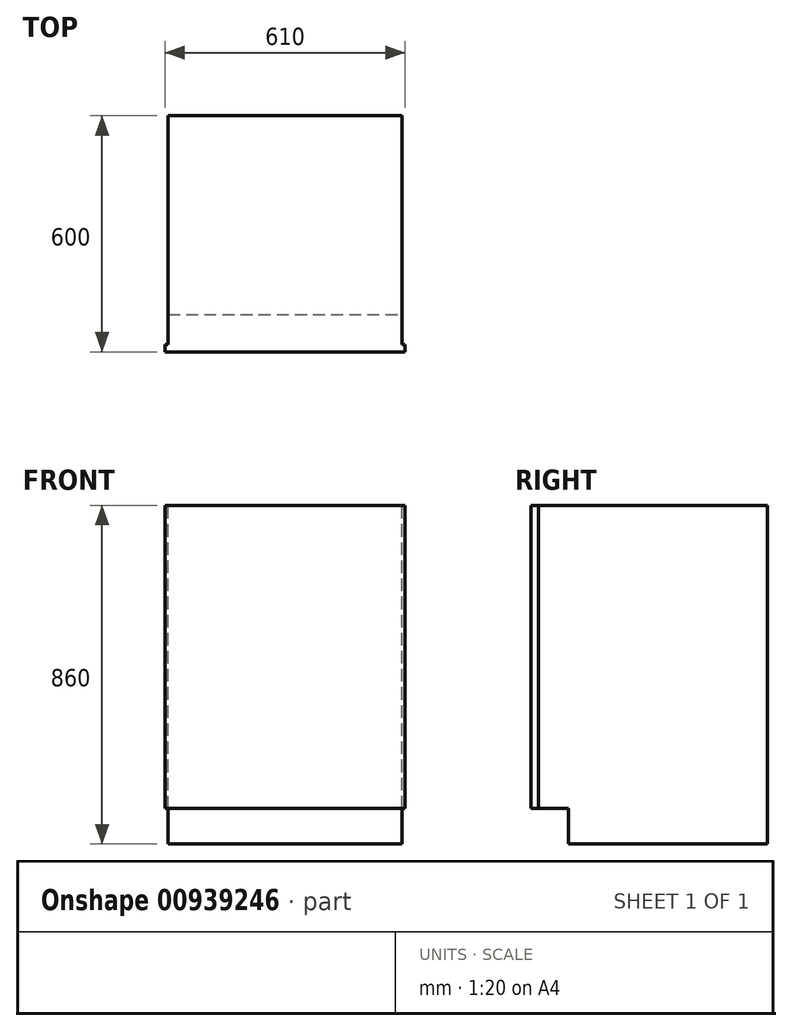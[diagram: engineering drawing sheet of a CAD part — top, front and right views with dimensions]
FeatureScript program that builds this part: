
annotation { "Feature Type Name" : "Feature", "Feature Type Description" : "" }
export const myFeature = defineFeature(function(context is Context, id is Id, definition is map)
    precondition{}
    {
        {
            var Q0;
            Q0=qCreatedBy(makeId("Front.planeOp"),FACE);
            var sketch = newSketch(context, id + "F0", { "sketchPlane" : qUnion([Q0])});
            skLineSegment(sketch, "E0.bottom", {"start": v(0, 0) * mm, "end": v(594, 0) * mm});
            skLineSegment(sketch, "E0.top", {"start": v(0, 860) * mm, "end": v(594, 860) * mm});
            skLineSegment(sketch, "E0.left", {"start": v(0, 0) * mm, "end": v(0, 860) * mm});
            skLineSegment(sketch, "E0.right", {"start": v(594, 0) * mm, "end": v(594, 860) * mm});
            skSolve(sketch);
        }
        {
            var Q0;
            Q0 = qSketchRegion(id + "F0", true);
            extrude(context, id + "F1", {"entities" : qUnion([Q0]), "depth" : 600 * mm, "offsetDistance" : 25 * mm});
        }
        {
            var Q0;
            Q0=makeQuery(id+"F1.opExtrude","CAP_FACE",FACE,{"disambiguationData":[OSD([sQuery(id+"F0.wireOp",EDGE,"E0.bottom"),sQuery(id+"F0.wireOp",EDGE,"E0.top"),sQuery(id+"F0.wireOp",EDGE,"E0.left"),sQuery(id+"F0.wireOp",EDGE,"E0.right")])],"isStart":false});
            var sketch = newSketch(context, id + "F2", { "sketchPlane" : qUnion([Q0])});
            skLineSegment(sketch, "E1.bottom", {"start": v(0, 0) * mm, "end": v(-8, 0) * mm});
            skLineSegment(sketch, "E1.top", {"start": v(0, 860) * mm, "end": v(-8, 860) * mm});
            skLineSegment(sketch, "E1.left", {"start": v(0, 0) * mm, "end": v(0, 860) * mm});
            skLineSegment(sketch, "E1.right", {"start": v(-8, 0) * mm, "end": v(-8, 860) * mm});
            skLineSegment(sketch, "E2", {"start": v(297, 0) * mm, "end": v(297, 939.39) * mm, "construction": true});
            skLineSegment(sketch, "E3.MirrorCS", {"start": v(602, 0) * mm, "end": v(602, 860) * mm});
            skLineSegment(sketch, "E4.MirrorCS", {"start": v(594, 860) * mm, "end": v(602, 860) * mm});
            skLineSegment(sketch, "E5.MirrorCS", {"start": v(594, 0) * mm, "end": v(594, 860) * mm});
            skLineSegment(sketch, "E6.MirrorCS", {"start": v(594, 0) * mm, "end": v(602, 0) * mm});
            skSolve(sketch);
        }
        {
            var Q0;
            Q0 = qSketchRegion(id + "F2", true);
            extrude(context, id + "F3", {"entities" : qUnion([Q0]), "operationType" : NewBodyOperationType.ADD, "oppositeDirection" : true, "depth" : 19 * mm, "offsetDistance" : 25 * mm});
        }
        {
            var Q0;
            Q0=makeQuery(id+"F3.boolean.opBoolean","MERGE",FACE,{"derivedFrom":[makeQuery(id+"F1.opExtrude","CAP_FACE",FACE,{"disambiguationData":[OSD([sQuery(id+"F0.wireOp",EDGE,"E0.bottom"),sQuery(id+"F0.wireOp",EDGE,"E0.top"),sQuery(id+"F0.wireOp",EDGE,"E0.left"),sQuery(id+"F0.wireOp",EDGE,"E0.right")])],"isStart":false}),makeQuery(id+"F3.opExtrude","CAP_FACE",FACE,{"disambiguationData":[OSD([sQuery(id+"F2.wireOp",EDGE,"E1.bottom"),sQuery(id+"F2.wireOp",EDGE,"E1.top"),sQuery(id+"F2.wireOp",EDGE,"E1.left"),sQuery(id+"F2.wireOp",EDGE,"E1.right")])],"isStart":true}),makeQuery(id+"F3.opExtrude","CAP_FACE",FACE,{"disambiguationData":[OSD([sQuery(id+"F2.wireOp",EDGE,"E3.MirrorCS"),sQuery(id+"F2.wireOp",EDGE,"E4.MirrorCS"),sQuery(id+"F2.wireOp",EDGE,"E5.MirrorCS"),sQuery(id+"F2.wireOp",EDGE,"E6.MirrorCS")])],"isStart":true})]});
            var sketch = newSketch(context, id + "F4", { "sketchPlane" : qUnion([Q0])});
            skLineSegment(sketch, "E7.bottom", {"start": v(-8, 0) * mm, "end": v(602, 0) * mm});
            skLineSegment(sketch, "E7.top", {"start": v(-8, 90) * mm, "end": v(602, 90) * mm});
            skLineSegment(sketch, "E7.left", {"start": v(-8, 0) * mm, "end": v(-8, 90) * mm});
            skLineSegment(sketch, "E7.right", {"start": v(602, 0) * mm, "end": v(602, 90) * mm});
            skSolve(sketch);
        }
        {
            var Q0;
            Q0 = qSketchRegion(id + "F4", true);
            extrude(context, id + "F5", {"entities" : qUnion([Q0]), "operationType" : NewBodyOperationType.REMOVE, "oppositeDirection" : true, "depth" : 95 * mm, "offsetDistance" : 25 * mm});
        }
    });
